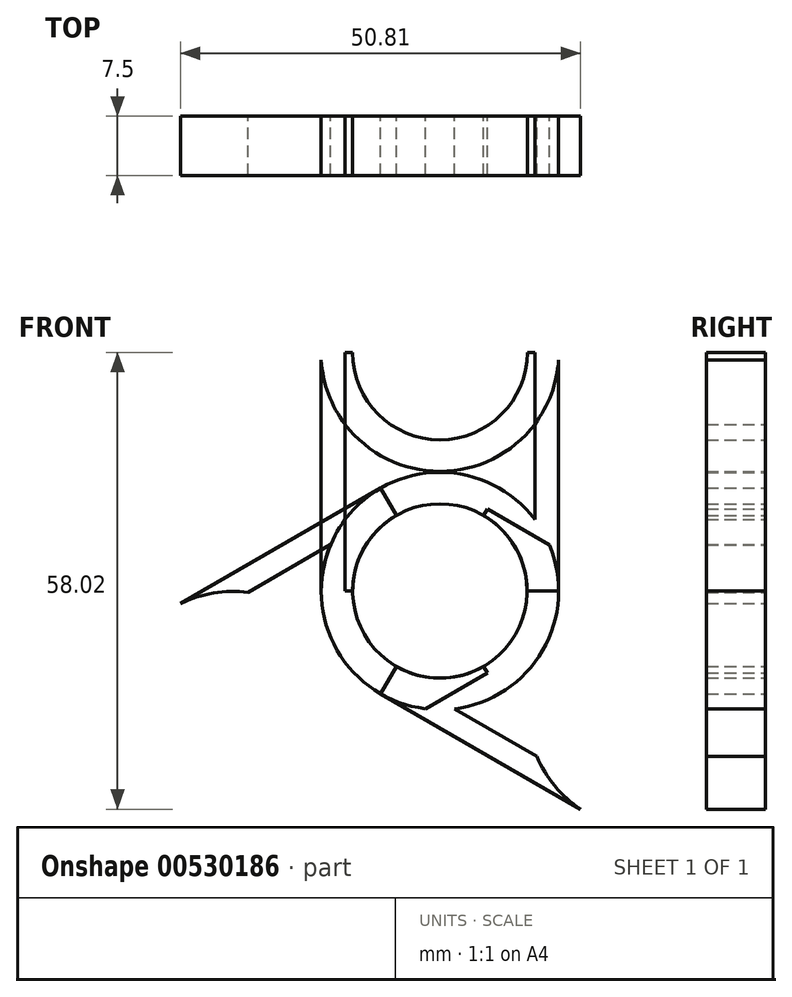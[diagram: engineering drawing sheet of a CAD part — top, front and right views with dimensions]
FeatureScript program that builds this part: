
annotation { "Feature Type Name" : "Feature", "Feature Type Description" : "" }
export const myFeature = defineFeature(function(context is Context, id is Id, definition is map)
    precondition{}
    {
        {
            var Q0;
            Q0=qCreatedBy(makeId("Front.planeOp"),FACE);
            var sketch = newSketch(context, id + "F0", { "sketchPlane" : qUnion([Q0])});
            skLineSegment(sketch, "E0.bottom", {"start": v(-15.07, 15.15) * mm, "end": v(15.07, 15.15) * mm});
            skLineSegment(sketch, "E0.top", {"start": v(-15.07, -15.15) * mm, "end": v(15.07, -15.15) * mm});
            skLineSegment(sketch, "E0.left", {"start": v(-15.07, 15.15) * mm, "end": v(-15.07, -15.15) * mm});
            skLineSegment(sketch, "E0.right", {"start": v(15.07, 15.15) * mm, "end": v(15.07, -15.15) * mm});
            skPoint(sketch, "E0.middle", {"position": v(0, 0) * mm});
            skLineSegment(sketch, "E1", {"start": v(-15.07, 0) * mm, "end": v(15.07, 0) * mm});
            skCircle(sketch, "E2", {"center": v(0, 15.15) * mm, "radius": 15.1 * mm});
            skCircle(sketch, "E3", {"center": v(0, -15.15) * mm, "radius": 15.07 * mm});
            skLineSegment(sketch, "E4", {"start": v(-15.07, -15.15) * mm, "end": v(-12.03, -15.15) * mm});
            skLineSegment(sketch, "E5", {"start": v(-12.03, -15.15) * mm, "end": v(-12.03, 15.15) * mm});
            skLineSegment(sketch, "E6", {"start": v(-12.03, 15.15) * mm, "end": v(-15.07, 15.15) * mm});
            skLineSegment(sketch, "E7", {"start": v(15.07, 15.15) * mm, "end": v(12.04, 15.15) * mm});
            skLineSegment(sketch, "E8", {"start": v(12.04, 15.15) * mm, "end": v(12.04, -15.15) * mm});
            skCircle(sketch, "E9", {"center": v(0, -15.15) * mm, "radius": 11.08 * mm});
            skCircle(sketch, "E10", {"center": v(0, 15.15) * mm, "radius": 11.09 * mm});
            skSolve(sketch);
        }
        {
            var Q0;
            {var subQ0=sQuery(id+"F0.wireOp",EDGE,"E6");Q0=makeQuery(id+"F0.imprint","IMPRINT",FACE,{"disambiguationData":[TD([[makeQuery(id+"F0.imprint","IMPRINT",EDGE,{"derivedFrom":subQ0}),-1.0]])]});}
            var Q1;
            {var subQ0=sQuery(id+"F0.wireOp",EDGE,"E1");var subQ1=sQuery(id+"F0.wireOp",EDGE,"E0.left");var subQ2=makeQuery(id+"F0.imprint","INTERSECT",VERTEX,{"derivedFrom":[subQ1,subQ0]});Q1=makeQuery(id+"F0.imprint","IMPRINT",FACE,{"disambiguationData":[TD([[makeQuery(id+"F0.imprint","IMPRINT",EDGE,{"disambiguationData":[TD([[subQ2,1.0]])],"derivedFrom":subQ1}),1.0]])]});}
            var Q2;
            {var subQ1=sQuery(id+"F0.wireOp",EDGE,"E0.left");var subQ3=sQuery(id+"F0.wireOp",EDGE,"E1");var subQ4=makeQuery(id+"F0.imprint","INTERSECT",VERTEX,{"derivedFrom":[subQ1,subQ3]});Q2=makeQuery(id+"F0.imprint","IMPRINT",FACE,{"disambiguationData":[TD([[makeQuery(id+"F0.imprint","IMPRINT",EDGE,{"disambiguationData":[TD([[subQ4,-1.0]])],"derivedFrom":subQ3}),-1.0]])]});}
            var Q3;
            {var subQ0=sQuery(id+"F0.wireOp",EDGE,"E8");var subQ5=sQuery(id+"F0.wireOp",EDGE,"E0.top");var subQ9=makeQuery(id+"F0.imprint","INTERSECT",VERTEX,{"derivedFrom":[subQ5,subQ0]});Q3=makeQuery(id+"F0.imprint","IMPRINT",FACE,{"disambiguationData":[TD([[makeQuery(id+"F0.imprint","IMPRINT",EDGE,{"disambiguationData":[TD([[subQ9,1.0]])],"derivedFrom":subQ5}),1.0]])]});}
            var Q4;
            {var subQ0=sQuery(id+"F0.wireOp",EDGE,"E4");Q4=makeQuery(id+"F0.imprint","IMPRINT",FACE,{"disambiguationData":[TD([[makeQuery(id+"F0.imprint","IMPRINT",EDGE,{"derivedFrom":subQ0}),1.0]])]});}
            var Q5;
            {var subQ6=sQuery(id+"F0.wireOp",EDGE,"E4");Q5=makeQuery(id+"F0.imprint","IMPRINT",FACE,{"disambiguationData":[TD([[makeQuery(id+"F0.imprint","IMPRINT",EDGE,{"derivedFrom":subQ6}),-1.0]])]});}
            var Q6;
            {var subQ1=sQuery(id+"F0.wireOp",EDGE,"E0.top");var subQ3=sQuery(id+"F0.wireOp",EDGE,"E8");var subQ4=makeQuery(id+"F0.imprint","INTERSECT",VERTEX,{"derivedFrom":[subQ1,subQ3]});Q6=makeQuery(id+"F0.imprint","IMPRINT",FACE,{"disambiguationData":[TD([[makeQuery(id+"F0.imprint","IMPRINT",EDGE,{"disambiguationData":[TD([[subQ4,1.0]])],"derivedFrom":subQ3}),1.0]])]});}
            var Q7;
            {var subQ1=sQuery(id+"F0.wireOp",EDGE,"E0.right");var subQ3=sQuery(id+"F0.wireOp",EDGE,"E1");var subQ4=makeQuery(id+"F0.imprint","INTERSECT",VERTEX,{"derivedFrom":[subQ1,subQ3]});Q7=makeQuery(id+"F0.imprint","IMPRINT",FACE,{"disambiguationData":[TD([[makeQuery(id+"F0.imprint","IMPRINT",EDGE,{"disambiguationData":[TD([[subQ4,1.0]])],"derivedFrom":subQ3}),-1.0]])]});}
            var Q8;
            {var subQ0=sQuery(id+"F0.wireOp",EDGE,"E1");var subQ1=sQuery(id+"F0.wireOp",EDGE,"E0.right");var subQ2=makeQuery(id+"F0.imprint","INTERSECT",VERTEX,{"derivedFrom":[subQ1,subQ0]});Q8=makeQuery(id+"F0.imprint","IMPRINT",FACE,{"disambiguationData":[TD([[makeQuery(id+"F0.imprint","IMPRINT",EDGE,{"disambiguationData":[TD([[subQ2,1.0]])],"derivedFrom":subQ1}),-1.0]])]});}
            var Q9;
            {var subQ0=sQuery(id+"F0.wireOp",EDGE,"E7");Q9=makeQuery(id+"F0.imprint","IMPRINT",FACE,{"disambiguationData":[TD([[makeQuery(id+"F0.imprint","IMPRINT",EDGE,{"derivedFrom":subQ0}),1.0]])]});}
            var Q10;
            {var subQ0=sQuery(id+"F0.wireOp",EDGE,"E5");var subQ3=sQuery(id+"F0.wireOp",EDGE,"E2");var subQ4=makeQuery(id+"F0.imprint","INTERSECT",VERTEX,{"derivedFrom":[subQ3,subQ0]});Q10=makeQuery(id+"F0.imprint","IMPRINT",FACE,{"disambiguationData":[TD([[makeQuery(id+"F0.imprint","IMPRINT",EDGE,{"disambiguationData":[TD([[subQ4,-1.0]])],"derivedFrom":subQ3}),1.0]])]});}
            var Q11;
            {var subQ0=sQuery(id+"F0.wireOp",EDGE,"E6");Q11=makeQuery(id+"F0.imprint","IMPRINT",FACE,{"disambiguationData":[TD([[makeQuery(id+"F0.imprint","IMPRINT",EDGE,{"derivedFrom":subQ0}),1.0]])]});}
            extrude(context, id + "F1", {"entities" : qUnion([Q0, Q1, Q2, Q3, Q4, Q5, Q6, Q7, Q8, Q9, Q10, Q11]), "depth" : 7.5 * mm, "offsetDistance" : 25 * mm});
        }
        {
            var Q0;
            Q0=makeQuery(id+"F1.opExtrude","SWEPT_BODY",BODY,{"disambiguationData":[OSD([sQuery(id+"F0.wireOp",EDGE,"E0.left"),sQuery(id+"F0.wireOp",EDGE,"E0.right"),sQuery(id+"F0.wireOp",EDGE,"E2"),sQuery(id+"F0.wireOp",EDGE,"E3"),sQuery(id+"F0.wireOp",EDGE,"E5"),sQuery(id+"F0.wireOp",EDGE,"E8"),sQuery(id+"F0.wireOp",EDGE,"E9"),sQuery(id+"F0.wireOp",EDGE,"E10")])]});
            var Q1;
            Q1=makeQuery(id+"F1.opExtrude","CAP_EDGE",EDGE,{"disambiguationData":[OSD([sQuery(id+"F0.wireOp",EDGE,"E9")])],"isStart":false});
            transform(context, id + "F2", {"entities" : qUnion([Q0]), "transformType" : TransformType.ROTATION, "transformAxis" : qUnion([Q1]), "angle" : 120 * degree, "makeCopy" : true});
        }
        {
            var Q0;
            Q0=makeQuery(id+"F2.opPattern","COPY",BODY,{"derivedFrom":makeQuery(id+"F1.opExtrude","SWEPT_BODY",BODY,{"disambiguationData":[OSD([sQuery(id+"F0.wireOp",EDGE,"E0.left"),sQuery(id+"F0.wireOp",EDGE,"E0.right"),sQuery(id+"F0.wireOp",EDGE,"E2"),sQuery(id+"F0.wireOp",EDGE,"E3"),sQuery(id+"F0.wireOp",EDGE,"E5"),sQuery(id+"F0.wireOp",EDGE,"E8"),sQuery(id+"F0.wireOp",EDGE,"E9"),sQuery(id+"F0.wireOp",EDGE,"E10")])]}),"instanceName":"1"});
            var Q1;
            Q1=makeQuery(id+"F1.opExtrude","CAP_EDGE",EDGE,{"disambiguationData":[OSD([sQuery(id+"F0.wireOp",EDGE,"E9")])],"isStart":false});
            transform(context, id + "F3", {"entities" : qUnion([Q0]), "transformType" : TransformType.ROTATION, "transformAxis" : qUnion([Q1]), "angle" : 120 * degree, "makeCopy" : true});
        }
    });
